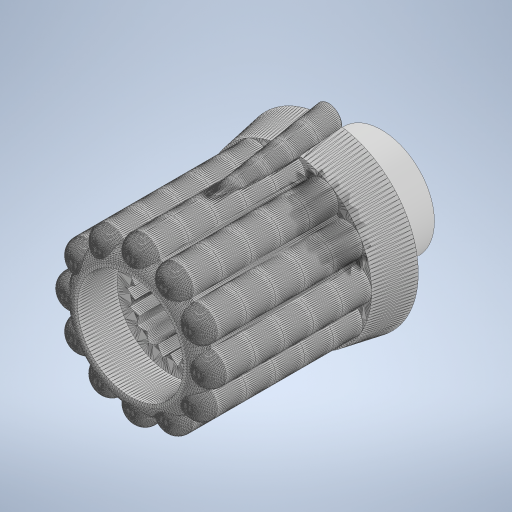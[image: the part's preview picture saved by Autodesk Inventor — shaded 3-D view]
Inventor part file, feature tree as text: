
AUTODESK INVENTOR PART (.ipt)
format: ipt  version: 2024 (Build 280153000, 153)  size: 751,616 bytes
history: native  units: mm
features: other x3, extrude x1, sketch x1
ambient origin geometry x8: Origin, YZ Plane, XZ Plane, XY Plane, X Axis, Y Axis, Z Axis, Center Point
bodies: Body1 (feature_tree)
feature tree (5):
  other  "Твердое тело1"
  other  "Volume_Cnob4"
  extrude  "Выдавливание1"  Depth=8.0mm
  sketch  "Эскиз1"
  other  "ЭлементСетки1"
